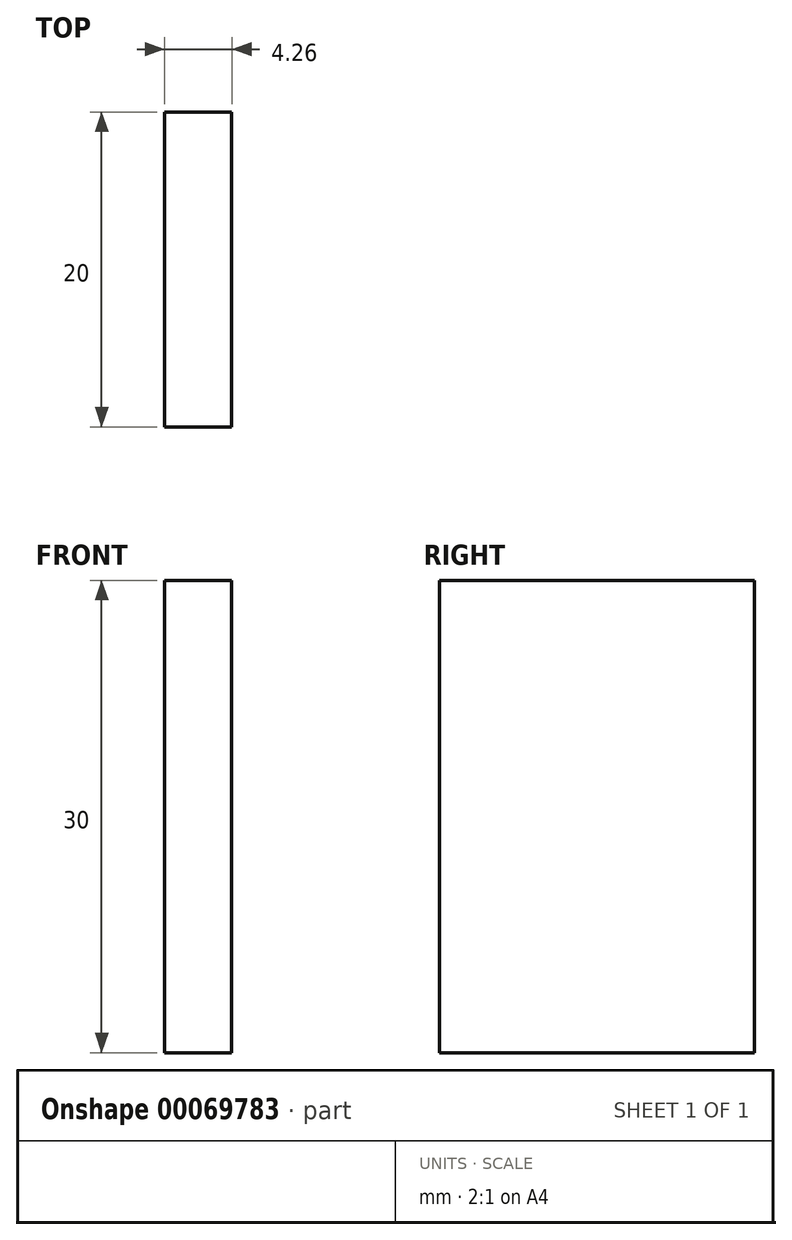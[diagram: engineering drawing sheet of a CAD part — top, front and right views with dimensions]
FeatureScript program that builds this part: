
annotation { "Feature Type Name" : "Feature", "Feature Type Description" : "" }
export const myFeature = defineFeature(function(context is Context, id is Id, definition is map)
    precondition{}
    {
        {
            var Q0;
            Q0=qCreatedBy(makeId("Front.planeOp"),FACE);
            var sketch = newSketch(context, id + "F0", { "sketchPlane" : qUnion([Q0])});
            skLineSegment(sketch, "E0.0", {"start": v(2.13, 2.62) * mm, "end": v(2.13, 32.62) * mm});
            skLineSegment(sketch, "E1.0", {"start": v(-2.13, 2.62) * mm, "end": v(-2.13, 32.62) * mm});
            skLineSegment(sketch, "E2", {"start": v(-2.13, 32.62) * mm, "end": v(2.13, 32.62) * mm});
            skLineSegment(sketch, "E3", {"start": v(-2.13, 2.62) * mm, "end": v(2.13, 2.62) * mm});
            skSolve(sketch);
        }
        {
            var Q0;
            Q0=makeQuery(id+"F0.imprint","IMPRINT",FACE,{"disambiguationData":[TD([[makeQuery(id+"F0.imprint","IMPRINT",EDGE,{"derivedFrom":sQuery(id+"F0.wireOp",EDGE,"E0.0")}),1.0]])]});
            extrude(context, id + "F1", {"entities" : qUnion([Q0]), "depth" : 20 * mm});
        }
    });
